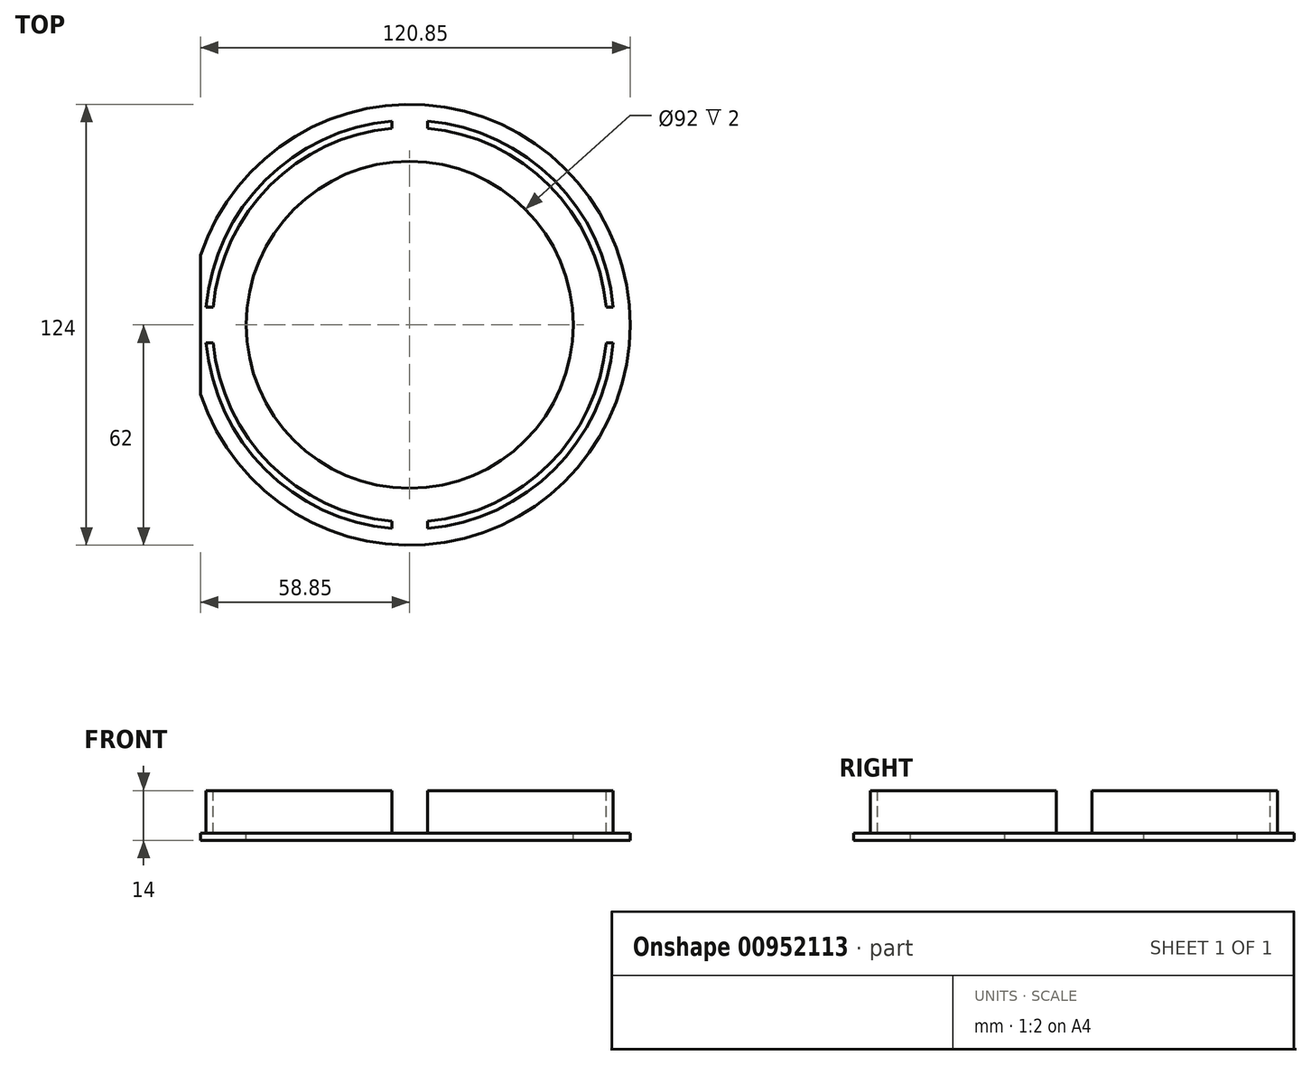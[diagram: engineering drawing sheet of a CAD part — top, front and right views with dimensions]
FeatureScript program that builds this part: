
annotation { "Feature Type Name" : "Feature", "Feature Type Description" : "" }
export const myFeature = defineFeature(function(context is Context, id is Id, definition is map)
    precondition{}
    {
        {
            var Q0;
            Q0=qCreatedBy(makeId("Top.planeOp"),FACE);
            var sketch = newSketch(context, id + "F0", { "sketchPlane" : qUnion([Q0])});
            skCircle(sketch, "E0", {"center": v(0, 0) * mm, "radius": 62 * mm});
            skSolve(sketch);
        }
        {
            var Q0;
            Q0 = qSketchRegion(id + "F0", true);
            extrude(context, id + "F1", {"entities" : qUnion([Q0]), "depth" : 2 * mm, "offsetDistance" : 25 * mm});
        }
        {
            var Q0;
            Q0=makeQuery(id+"F1.opExtrude","CAP_FACE",FACE,{"disambiguationData":[OSD([sQuery(id+"F0.wireOp",EDGE,"E0")])],"isStart":false});
            var sketch = newSketch(context, id + "F2", { "sketchPlane" : qUnion([Q0])});
            skCircle(sketch, "E1", {"center": v(0, 0) * mm, "radius": 57.5 * mm});
            skSolve(sketch);
        }
        {
            var Q0;
            Q0 = qSketchRegion(id + "F2", true);
            extrude(context, id + "F3", {"entities" : qUnion([Q0]), "operationType" : NewBodyOperationType.ADD, "depth" : 12 * mm, "offsetDistance" : 25 * mm});
        }
        {
            var Q0;
            Q0=makeQuery(id+"F3.opExtrude","CAP_FACE",FACE,{"disambiguationData":[OSD([sQuery(id+"F2.wireOp",EDGE,"E1")])],"isStart":false});
            var sketch = newSketch(context, id + "F4", { "sketchPlane" : qUnion([Q0])});
            skCircle(sketch, "E2", {"center": v(0, 0) * mm, "radius": 55.5 * mm});
            skSolve(sketch);
        }
        {
            var Q0;
            Q0 = qSketchRegion(id + "F4", true);
            extrude(context, id + "F5", {"entities" : qUnion([Q0]), "operationType" : NewBodyOperationType.REMOVE, "oppositeDirection" : true, "depth" : 12 * mm, "offsetDistance" : 25 * mm});
        }
        {
            var Q0;
            Q0=makeQuery(id+"F5.boolean.opBoolean","COPY",FACE,{"derivedFrom":makeQuery(id+"F5.opExtrude","CAP_FACE",FACE,{"disambiguationData":[OSD([sQuery(id+"F4.wireOp",EDGE,"E2")])],"isStart":false})});
            var sketch = newSketch(context, id + "F6", { "sketchPlane" : qUnion([Q0])});
            skCircle(sketch, "E3", {"center": v(0, 0) * mm, "radius": 46 * mm});
            skSolve(sketch);
        }
        {
            var Q0;
            Q0 = qSketchRegion(id + "F6", true);
            extrude(context, id + "F7", {"entities" : qUnion([Q0]), "operationType" : NewBodyOperationType.REMOVE, "oppositeDirection" : true, "depth" : 25 * mm, "offsetDistance" : 25 * mm});
        }
        {
            var Q0;
            Q0=makeQuery(id+"F1.opExtrude","CAP_FACE",FACE,{"disambiguationData":[OSD([sQuery(id+"F0.wireOp",EDGE,"E0")])],"isStart":false});
            var sketch = newSketch(context, id + "F8", { "sketchPlane" : qUnion([Q0])});
            skLineSegment(sketch, "E4.bottom", {"start": v(-72.95, 40.58) * mm, "end": v(-58.85, 40.58) * mm});
            skLineSegment(sketch, "E4.top", {"start": v(-72.95, -45.22) * mm, "end": v(-58.85, -45.22) * mm});
            skLineSegment(sketch, "E4.left", {"start": v(-72.95, 40.58) * mm, "end": v(-72.95, -45.22) * mm});
            skLineSegment(sketch, "E4.right", {"start": v(-58.85, 40.58) * mm, "end": v(-58.85, -45.22) * mm});
            skSolve(sketch);
        }
        {
            var Q0;
            Q0 = qSketchRegion(id + "F8", true);
            extrude(context, id + "F9", {"entities" : qUnion([Q0]), "operationType" : NewBodyOperationType.REMOVE, "oppositeDirection" : true, "depth" : 25 * mm, "offsetDistance" : 25 * mm});
        }
        {
            var Q0;
            Q0=makeQuery(id+"F3.opExtrude","CAP_FACE",FACE,{"disambiguationData":[OSD([sQuery(id+"F2.wireOp",EDGE,"E1")])],"isStart":false});
            var sketch = newSketch(context, id + "F10", { "sketchPlane" : qUnion([Q0])});
            skLineSegment(sketch, "E5.bottom", {"start": v(-5, 70) * mm, "end": v(5, 70) * mm});
            skLineSegment(sketch, "E5.top", {"start": v(-5, -70) * mm, "end": v(5, -70) * mm});
            skLineSegment(sketch, "E5.left", {"start": v(-5, 70) * mm, "end": v(-5, -70) * mm});
            skLineSegment(sketch, "E5.right", {"start": v(5, 70) * mm, "end": v(5, -70) * mm});
            skPoint(sketch, "E5.middle", {"position": v(0, 0) * mm});
            skSolve(sketch);
        }
        {
            var Q0;
            Q0 = qSketchRegion(id + "F10", true);
            extrude(context, id + "F11", {"entities" : qUnion([Q0]), "operationType" : NewBodyOperationType.REMOVE, "oppositeDirection" : true, "depth" : 12 * mm, "offsetDistance" : 25 * mm});
        }
        {
            var Q0;
            {var subQ0=sQuery(id+"F2.wireOp",EDGE,"E1");Q0=makeQuery(id+"F11.boolean.opBoolean","SPLIT",FACE,{"disambiguationData":[TD([makeQuery(id+"F11.opExtrude","SWEPT_FACE",FACE,{"disambiguationData":[OSD([sQuery(id+"F10.wireOp",EDGE,"E5.left")])]})])],"derivedFrom":makeQuery(id+"F3.opExtrude","CAP_FACE",FACE,{"disambiguationData":[OSD([subQ0])],"isStart":false})});}
            var sketch = newSketch(context, id + "F12", { "sketchPlane" : qUnion([Q0])});
            skLineSegment(sketch, "E6.bottom", {"start": v(-94.67, 5) * mm, "end": v(94.67, 5) * mm});
            skLineSegment(sketch, "E6.top", {"start": v(-94.67, -5) * mm, "end": v(94.67, -5) * mm});
            skLineSegment(sketch, "E6.left", {"start": v(-94.67, 5) * mm, "end": v(-94.67, -5) * mm});
            skLineSegment(sketch, "E6.right", {"start": v(94.67, 5) * mm, "end": v(94.67, -5) * mm});
            skPoint(sketch, "E6.middle", {"position": v(0, 0) * mm});
            skSolve(sketch);
        }
        {
            var Q0;
            Q0 = qSketchRegion(id + "F12", true);
            extrude(context, id + "F13", {"entities" : qUnion([Q0]), "operationType" : NewBodyOperationType.REMOVE, "oppositeDirection" : true, "depth" : 12 * mm, "offsetDistance" : 25 * mm});
        }
    });
